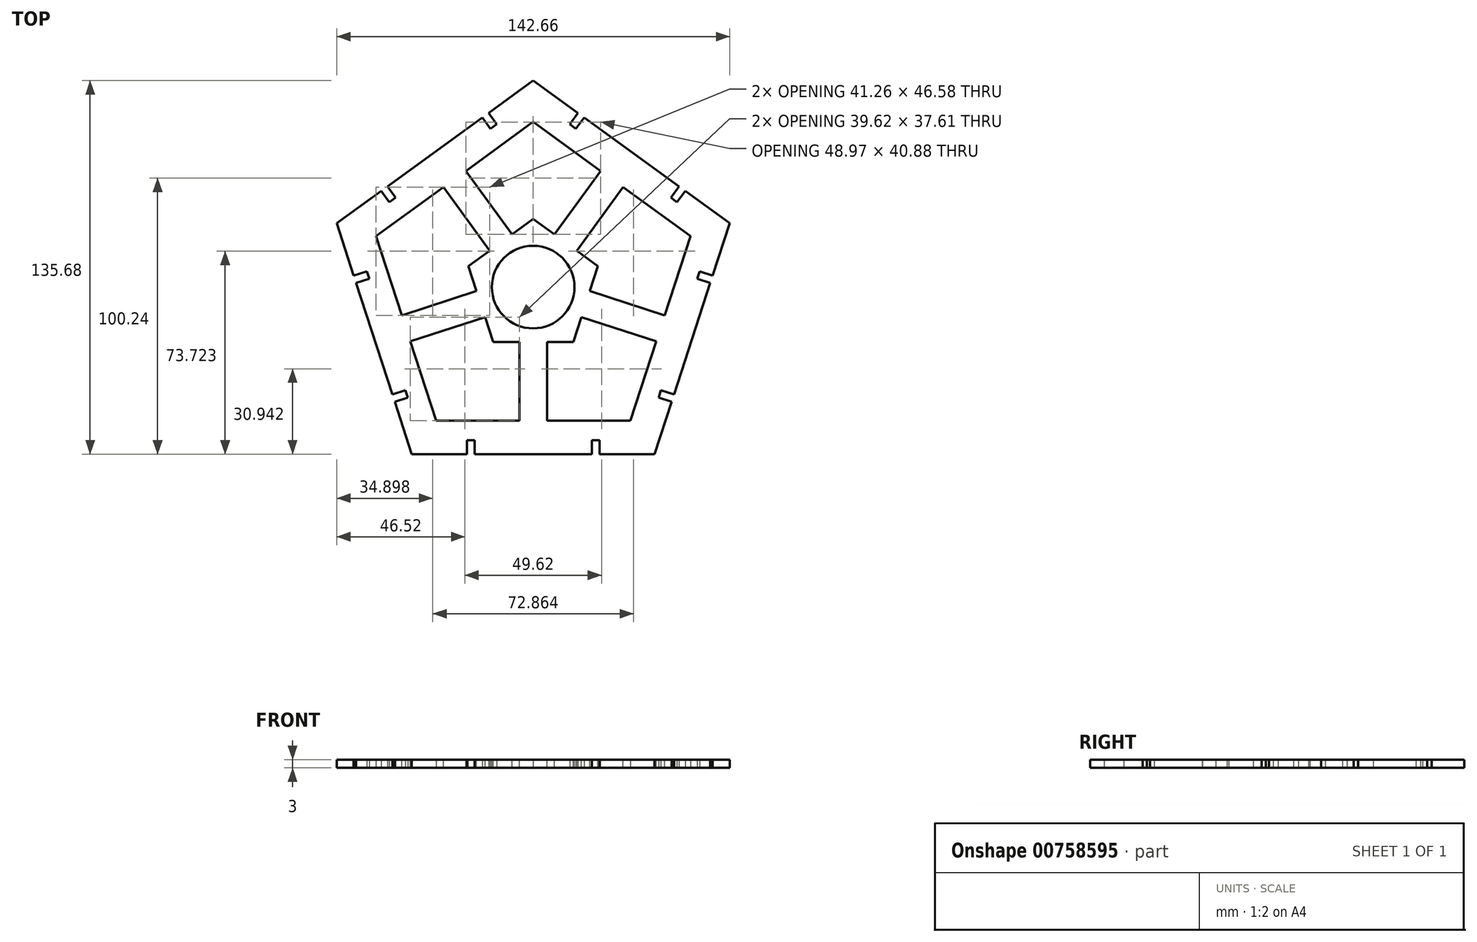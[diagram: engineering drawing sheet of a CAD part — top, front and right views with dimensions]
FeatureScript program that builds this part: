
annotation { "Feature Type Name" : "Feature", "Feature Type Description" : "" }
export const myFeature = defineFeature(function(context is Context, id is Id, definition is map)
    precondition{}
    {
        {
            var Q0;
            Q0=qCreatedBy(makeId("Top.planeOp"),FACE);
            var sketch = newSketch(context, id + "F0", { "sketchPlane" : qUnion([Q0])});
            skCircle(sketch, "E0.cCircle", {"center": v(0, 0) * mm, "radius": 75 * mm, "construction": true});
            skLineSegment(sketch, "E0.0", {"start": v(0, 75) * mm, "end": v(16.18, 63.24) * mm});
            skLineSegment(sketch, "E0.1", {"start": v(71.33, 23.18) * mm, "end": v(65.15, 4.16) * mm});
            skLineSegment(sketch, "E0.2", {"start": v(44.08, -60.68) * mm, "end": v(24.08, -60.68) * mm});
            skLineSegment(sketch, "E0.3", {"start": v(-44.08, -60.68) * mm, "end": v(-50.26, -41.66) * mm});
            skLineSegment(sketch, "E0.4", {"start": v(-71.33, 23.18) * mm, "end": v(-55.15, 34.93) * mm});
            skLineSegment(sketch, "E1", {"start": v(-16.18, 63.24) * mm, "end": v(-13.24, 59.2) * mm});
            skLineSegment(sketch, "E2", {"start": v(-13.24, 59.2) * mm, "end": v(-15.5, 57.55) * mm});
            skLineSegment(sketch, "E3", {"start": v(-15.5, 57.55) * mm, "end": v(-18.45, 61.6) * mm});
            skLineSegment(sketch, "E4", {"start": v(-35.66, 49.09) * mm, "end": v(44.08, -60.68) * mm, "construction": true});
            skLineSegment(sketch, "E5", {"start": v(-44.08, -60.68) * mm, "end": v(35.66, 49.09) * mm, "construction": true});
            skLineSegment(sketch, "E6", {"start": v(-71.33, 23.18) * mm, "end": v(57.7, -18.75) * mm, "construction": true});
            skLineSegment(sketch, "E7", {"start": v(71.33, 23.18) * mm, "end": v(-57.7, -18.75) * mm, "construction": true});
            skLineSegment(sketch, "E8", {"start": v(0, 75) * mm, "end": v(0, -60.68) * mm, "construction": true});
            skLineSegment(sketch, "E9.trimOffspring", {"start": v(-16.18, 63.24) * mm, "end": v(0, 75) * mm});
            skLineSegment(sketch, "E10.MirrorCS", {"start": v(-55.15, 34.93) * mm, "end": v(-52.2, 30.89) * mm});
            skLineSegment(sketch, "E11.MirrorCS", {"start": v(-49.94, 32.53) * mm, "end": v(-52.88, 36.58) * mm});
            skLineSegment(sketch, "E12.MirrorCS", {"start": v(-52.2, 30.89) * mm, "end": v(-49.94, 32.53) * mm});
            skLineSegment(sketch, "E13.trimOffspring", {"start": v(-52.88, 36.58) * mm, "end": v(-18.45, 61.6) * mm});
            skLineSegment(sketch, "E14.1.0", {"start": v(-65.15, 4.16) * mm, "end": v(-60.4, 5.7) * mm});
            skLineSegment(sketch, "E14.1.1", {"start": v(-59.53, 3.04) * mm, "end": v(-64.28, 1.5) * mm});
            skLineSegment(sketch, "E14.1.2", {"start": v(-60.4, 5.7) * mm, "end": v(-59.53, 3.04) * mm});
            skLineSegment(sketch, "E14.1.3", {"start": v(-46.37, -37.45) * mm, "end": v(-51.13, -39) * mm});
            skLineSegment(sketch, "E14.1.4", {"start": v(-45.5, -40.11) * mm, "end": v(-46.37, -37.45) * mm});
            skLineSegment(sketch, "E14.1.5", {"start": v(-50.26, -41.66) * mm, "end": v(-45.5, -40.11) * mm});
            skLineSegment(sketch, "E14.2.0", {"start": v(-24.08, -60.68) * mm, "end": v(-24.08, -55.68) * mm});
            skLineSegment(sketch, "E14.2.1", {"start": v(-21.28, -55.68) * mm, "end": v(-21.28, -60.68) * mm});
            skLineSegment(sketch, "E14.2.2", {"start": v(-24.08, -55.68) * mm, "end": v(-21.28, -55.68) * mm});
            skLineSegment(sketch, "E14.2.3", {"start": v(21.28, -55.68) * mm, "end": v(21.28, -60.68) * mm});
            skLineSegment(sketch, "E14.2.4", {"start": v(24.08, -55.68) * mm, "end": v(21.28, -55.68) * mm});
            skLineSegment(sketch, "E14.2.5", {"start": v(24.08, -60.68) * mm, "end": v(24.08, -55.68) * mm});
            skLineSegment(sketch, "E14.3.0", {"start": v(50.26, -41.66) * mm, "end": v(45.5, -40.11) * mm});
            skLineSegment(sketch, "E14.3.1", {"start": v(46.37, -37.45) * mm, "end": v(51.13, -39) * mm});
            skLineSegment(sketch, "E14.3.2", {"start": v(45.5, -40.11) * mm, "end": v(46.37, -37.45) * mm});
            skLineSegment(sketch, "E14.3.3", {"start": v(59.53, 3.04) * mm, "end": v(64.28, 1.5) * mm});
            skLineSegment(sketch, "E14.3.4", {"start": v(60.4, 5.7) * mm, "end": v(59.53, 3.04) * mm});
            skLineSegment(sketch, "E14.3.5", {"start": v(65.15, 4.16) * mm, "end": v(60.4, 5.7) * mm});
            skLineSegment(sketch, "E14.4.0", {"start": v(55.15, 34.93) * mm, "end": v(52.2, 30.89) * mm});
            skLineSegment(sketch, "E14.4.1", {"start": v(49.94, 32.53) * mm, "end": v(52.88, 36.58) * mm});
            skLineSegment(sketch, "E14.4.2", {"start": v(52.2, 30.89) * mm, "end": v(49.94, 32.53) * mm});
            skLineSegment(sketch, "E14.4.3", {"start": v(15.5, 57.55) * mm, "end": v(18.45, 61.6) * mm});
            skLineSegment(sketch, "E14.4.4", {"start": v(13.24, 59.2) * mm, "end": v(15.5, 57.55) * mm});
            skLineSegment(sketch, "E14.4.5", {"start": v(16.18, 63.24) * mm, "end": v(13.24, 59.2) * mm});
            skLineSegment(sketch, "E15.trimOffspring", {"start": v(-65.15, 4.16) * mm, "end": v(-71.33, 23.18) * mm});
            skLineSegment(sketch, "E16.trimOffspring", {"start": v(21.28, -60.68) * mm, "end": v(-21.28, -60.68) * mm});
            skLineSegment(sketch, "E17.trimOffspring", {"start": v(-24.08, -60.68) * mm, "end": v(-44.08, -60.68) * mm});
            skLineSegment(sketch, "E18.trimOffspring", {"start": v(-51.13, -39) * mm, "end": v(-64.28, 1.5) * mm});
            skLineSegment(sketch, "E19.trimOffspring", {"start": v(18.45, 61.6) * mm, "end": v(52.88, 36.58) * mm});
            skLineSegment(sketch, "E20.trimOffspring", {"start": v(55.15, 34.93) * mm, "end": v(71.33, 23.18) * mm});
            skLineSegment(sketch, "E21.trimOffspring", {"start": v(64.28, 1.5) * mm, "end": v(51.13, -39) * mm});
            skLineSegment(sketch, "E22.trimOffspring", {"start": v(50.26, -41.66) * mm, "end": v(44.08, -60.68) * mm});
            skCircle(sketch, "E23.cCircle", {"center": v(0, 0) * mm, "radius": 60 * mm, "construction": true});
            skLineSegment(sketch, "E23.0", {"start": v(0, 60) * mm, "end": v(57.06, 18.54) * mm});
            skLineSegment(sketch, "E23.1", {"start": v(57.06, 18.54) * mm, "end": v(35.27, -48.54) * mm});
            skLineSegment(sketch, "E23.2", {"start": v(35.27, -48.54) * mm, "end": v(-35.27, -48.54) * mm});
            skLineSegment(sketch, "E23.3", {"start": v(-35.27, -48.54) * mm, "end": v(-57.06, 18.54) * mm});
            skLineSegment(sketch, "E23.4", {"start": v(-57.06, 18.54) * mm, "end": v(0, 60) * mm});
            skSolve(sketch);
        }
        {
            var Q0;
            Q0=qSketchRegion(id+"F0",true);
            extrude(context, id + "F1", {"entities" : qUnion([Q0]), "depth" : 3 * mm, "offsetDistance" : 25 * mm});
        }
        {
            var Q0;
            Q0=makeQuery(id+"F7oamPH84VVUofO_3.boolean.opBoolean","MERGE",FACE,{"derivedFrom":[makeQuery(id+"F9TRZGhlL7vivvJ_2.boolean.opBoolean","MERGE",FACE,{"derivedFrom":[makeQuery(id+"FcwpvQgZIup3No6_1.boolean.opBoolean","MERGE",FACE,{"derivedFrom":[makeQuery(id+"F1.opExtrude","CAP_FACE",FACE,{"disambiguationData":[OSD([sQuery(id+"F0.wireOp",EDGE,"E0.0"),sQuery(id+"F0.wireOp",EDGE,"E0.1"),sQuery(id+"F0.wireOp",EDGE,"E0.2"),sQuery(id+"F0.wireOp",EDGE,"E0.3"),sQuery(id+"F0.wireOp",EDGE,"E0.4"),sQuery(id+"F0.wireOp",EDGE,"E1"),sQuery(id+"F0.wireOp",EDGE,"E2"),sQuery(id+"F0.wireOp",EDGE,"E3"),sQuery(id+"F0.wireOp",EDGE,"E9.trimOffspring"),sQuery(id+"F0.wireOp",EDGE,"E10.MirrorCS"),sQuery(id+"F0.wireOp",EDGE,"E11.MirrorCS"),sQuery(id+"F0.wireOp",EDGE,"E12.MirrorCS"),sQuery(id+"F0.wireOp",EDGE,"E13.trimOffspring"),sQuery(id+"F0.wireOp",EDGE,"E14.1.0"),sQuery(id+"F0.wireOp",EDGE,"E14.1.1"),sQuery(id+"F0.wireOp",EDGE,"E14.1.2"),sQuery(id+"F0.wireOp",EDGE,"E14.1.3"),sQuery(id+"F0.wireOp",EDGE,"E14.1.4"),sQuery(id+"F0.wireOp",EDGE,"E14.1.5"),sQuery(id+"F0.wireOp",EDGE,"E14.2.0"),sQuery(id+"F0.wireOp",EDGE,"E14.2.1"),sQuery(id+"F0.wireOp",EDGE,"E14.2.2"),sQuery(id+"F0.wireOp",EDGE,"E14.2.3"),sQuery(id+"F0.wireOp",EDGE,"E14.2.4"),sQuery(id+"F0.wireOp",EDGE,"E14.2.5"),sQuery(id+"F0.wireOp",EDGE,"E14.3.0"),sQuery(id+"F0.wireOp",EDGE,"E14.3.1"),sQuery(id+"F0.wireOp",EDGE,"E14.3.2"),sQuery(id+"F0.wireOp",EDGE,"E14.3.3"),sQuery(id+"F0.wireOp",EDGE,"E14.3.4"),sQuery(id+"F0.wireOp",EDGE,"E14.3.5"),sQuery(id+"F0.wireOp",EDGE,"E14.4.0"),sQuery(id+"F0.wireOp",EDGE,"E14.4.1"),sQuery(id+"F0.wireOp",EDGE,"E14.4.2"),sQuery(id+"F0.wireOp",EDGE,"E14.4.3"),sQuery(id+"F0.wireOp",EDGE,"E14.4.4"),sQuery(id+"F0.wireOp",EDGE,"E14.4.5"),sQuery(id+"F0.wireOp",EDGE,"E15.trimOffspring"),sQuery(id+"F0.wireOp",EDGE,"E16.trimOffspring"),sQuery(id+"F0.wireOp",EDGE,"E17.trimOffspring"),sQuery(id+"F0.wireOp",EDGE,"E18.trimOffspring"),sQuery(id+"F0.wireOp",EDGE,"E19.trimOffspring"),sQuery(id+"F0.wireOp",EDGE,"E20.trimOffspring"),sQuery(id+"F0.wireOp",EDGE,"E21.trimOffspring"),sQuery(id+"F0.wireOp",EDGE,"E22.trimOffspring"),sQuery(id+"F0.wireOp",EDGE,"E23.0"),sQuery(id+"F0.wireOp",EDGE,"E23.1"),sQuery(id+"F0.wireOp",EDGE,"E23.2"),sQuery(id+"F0.wireOp",EDGE,"E23.3"),sQuery(id+"F0.wireOp",EDGE,"E23.4")])],"isStart":false}),makeQuery(id+"FcwpvQgZIup3No6_1.opExtrude","CAP_FACE",FACE,{"disambiguationData":[OSD([sQuery(id+"FsdsBESLdJ1JIvc_1.wireOp",EDGE,"de833a3a-313a-4596-8202-035c041a42ca.0"),sQuery(id+"FsdsBESLdJ1JIvc_1.wireOp",EDGE,"de833a3a-313a-4596-8202-035c041a42ca.1"),sQuery(id+"FsdsBESLdJ1JIvc_1.wireOp",EDGE,"de833a3a-313a-4596-8202-035c041a42ca.2"),sQuery(id+"FsdsBESLdJ1JIvc_1.wireOp",EDGE,"de833a3a-313a-4596-8202-035c041a42ca.3"),sQuery(id+"FsdsBESLdJ1JIvc_1.wireOp",EDGE,"de833a3a-313a-4596-8202-035c041a42ca.4"),sQuery(id+"FsdsBESLdJ1JIvc_1.wireOp",EDGE,"a308593b-41e8-415b-b94c-e11fd7466d5a.0"),sQuery(id+"FsdsBESLdJ1JIvc_1.wireOp",EDGE,"a308593b-41e8-415b-b94c-e11fd7466d5a.1"),sQuery(id+"FsdsBESLdJ1JIvc_1.wireOp",EDGE,"a308593b-41e8-415b-b94c-e11fd7466d5a.2"),sQuery(id+"FsdsBESLdJ1JIvc_1.wireOp",EDGE,"a308593b-41e8-415b-b94c-e11fd7466d5a.3"),sQuery(id+"FsdsBESLdJ1JIvc_1.wireOp",EDGE,"a308593b-41e8-415b-b94c-e11fd7466d5a.4")])],"isStart":true})]}),makeQuery(id+"F9TRZGhlL7vivvJ_2.opExtrude","CAP_FACE",FACE,{"disambiguationData":[OSD([sQuery(id+"Ff6WRs0W7eyaktz_2.wireOp",EDGE,"6beabe26-07f1-4b03-9cb5-d80d9ebc594f.0"),sQuery(id+"Ff6WRs0W7eyaktz_2.wireOp",EDGE,"6beabe26-07f1-4b03-9cb5-d80d9ebc594f.1"),sQuery(id+"Ff6WRs0W7eyaktz_2.wireOp",EDGE,"6beabe26-07f1-4b03-9cb5-d80d9ebc594f.2"),sQuery(id+"Ff6WRs0W7eyaktz_2.wireOp",EDGE,"6beabe26-07f1-4b03-9cb5-d80d9ebc594f.3"),sQuery(id+"Ff6WRs0W7eyaktz_2.wireOp",EDGE,"6beabe26-07f1-4b03-9cb5-d80d9ebc594f.4"),sQuery(id+"Ff6WRs0W7eyaktz_2.wireOp",EDGE,"313384f4-31bd-43dd-b64d-91ce542deea2.0"),sQuery(id+"Ff6WRs0W7eyaktz_2.wireOp",EDGE,"313384f4-31bd-43dd-b64d-91ce542deea2.1"),sQuery(id+"Ff6WRs0W7eyaktz_2.wireOp",EDGE,"313384f4-31bd-43dd-b64d-91ce542deea2.2"),sQuery(id+"Ff6WRs0W7eyaktz_2.wireOp",EDGE,"313384f4-31bd-43dd-b64d-91ce542deea2.3"),sQuery(id+"Ff6WRs0W7eyaktz_2.wireOp",EDGE,"313384f4-31bd-43dd-b64d-91ce542deea2.4")])],"isStart":true})]}),makeQuery(id+"F7oamPH84VVUofO_3.opExtrude","CAP_FACE",FACE,{"disambiguationData":[OSD([sQuery(id+"FCtNTOOhJTabHIr_3.wireOp",EDGE,"ce65d7c0-cc87-4925-8475-852a1e82e0af.0"),sQuery(id+"FCtNTOOhJTabHIr_3.wireOp",EDGE,"ce65d7c0-cc87-4925-8475-852a1e82e0af.1"),sQuery(id+"FCtNTOOhJTabHIr_3.wireOp",EDGE,"ce65d7c0-cc87-4925-8475-852a1e82e0af.2"),sQuery(id+"FCtNTOOhJTabHIr_3.wireOp",EDGE,"ce65d7c0-cc87-4925-8475-852a1e82e0af.3"),sQuery(id+"FCtNTOOhJTabHIr_3.wireOp",EDGE,"ce65d7c0-cc87-4925-8475-852a1e82e0af.4"),sQuery(id+"FCtNTOOhJTabHIr_3.wireOp",EDGE,"5047fc87-8845-4384-a8f3-4e3b16de0bd1.0"),sQuery(id+"FCtNTOOhJTabHIr_3.wireOp",EDGE,"5047fc87-8845-4384-a8f3-4e3b16de0bd1.1"),sQuery(id+"FCtNTOOhJTabHIr_3.wireOp",EDGE,"5047fc87-8845-4384-a8f3-4e3b16de0bd1.2"),sQuery(id+"FCtNTOOhJTabHIr_3.wireOp",EDGE,"5047fc87-8845-4384-a8f3-4e3b16de0bd1.3"),sQuery(id+"FCtNTOOhJTabHIr_3.wireOp",EDGE,"5047fc87-8845-4384-a8f3-4e3b16de0bd1.4")])],"isStart":true})]});
            var sketch = newSketch(context, id + "F2", { "sketchPlane" : qUnion([Q0])});
            skLineSegment(sketch, "E24.0", {"start": v(14.53, -20) * mm, "end": v(5, -20) * mm});
            skLineSegment(sketch, "E24.1", {"start": v(-14.53, -20) * mm, "end": v(-17.48, -10.94) * mm});
            skLineSegment(sketch, "E24.2", {"start": v(-23.51, 7.64) * mm, "end": v(-15.8, 13.24) * mm});
            skLineSegment(sketch, "E24.3", {"start": v(0, 24.72) * mm, "end": v(7.71, 19.12) * mm});
            skLineSegment(sketch, "E24.4", {"start": v(23.51, 7.64) * mm, "end": v(20.57, -1.43) * mm});
            skPoint(sketch, "E24.0.midPoint", {"position": v(0, -20) * mm});
            skCircle(sketch, "E25", {"center": v(0, 0) * mm, "radius": 15 * mm});
            skLineSegment(sketch, "E26", {"start": v(-11.76, 16.18) * mm, "end": v(-28.53, 39.27) * mm, "construction": true});
            skLineSegment(sketch, "E27", {"start": v(-7.71, 19.12) * mm, "end": v(-24.49, 42.2) * mm});
            skLineSegment(sketch, "E28.MirrorCS", {"start": v(-15.8, 13.24) * mm, "end": v(-32.58, 36.33) * mm});
            skLineSegment(sketch, "E29", {"start": v(-24.49, 42.2) * mm, "end": v(-32.58, 36.33) * mm});
            skLineSegment(sketch, "E30.trimOffspring", {"start": v(-7.71, 19.12) * mm, "end": v(0, 24.72) * mm});
            skLineSegment(sketch, "E31.1.0", {"start": v(-20.57, -1.43) * mm, "end": v(-47.71, -10.24) * mm});
            skLineSegment(sketch, "E31.1.1", {"start": v(-17.48, -10.94) * mm, "end": v(-44.62, -19.76) * mm});
            skLineSegment(sketch, "E31.1.2", {"start": v(-47.71, -10.24) * mm, "end": v(-44.62, -19.76) * mm});
            skCircle(sketch, "E31.1.3", {"center": v(0, 0) * mm, "radius": 20 * mm, "construction": true});
            skLineSegment(sketch, "E31.2.0", {"start": v(-5, -20) * mm, "end": v(-5, -48.54) * mm});
            skLineSegment(sketch, "E31.2.1", {"start": v(5, -20) * mm, "end": v(5, -48.54) * mm});
            skLineSegment(sketch, "E31.2.2", {"start": v(-5, -48.54) * mm, "end": v(5, -48.54) * mm});
            skLineSegment(sketch, "E31.3.0", {"start": v(17.48, -10.94) * mm, "end": v(44.62, -19.76) * mm});
            skLineSegment(sketch, "E31.3.1", {"start": v(20.57, -1.43) * mm, "end": v(47.71, -10.24) * mm});
            skLineSegment(sketch, "E31.3.2", {"start": v(44.62, -19.76) * mm, "end": v(47.71, -10.24) * mm});
            skArc(sketch, "E31.3.3", {"start": v(-11.76, 16.18) * mm, "mid": v(-19.75, 3.13) * mm, "end": v(-16.18, -11.76) * mm, "construction": true});
            skLineSegment(sketch, "E31.4.0", {"start": v(15.8, 13.24) * mm, "end": v(32.58, 36.33) * mm});
            skLineSegment(sketch, "E31.4.1", {"start": v(7.71, 19.12) * mm, "end": v(24.49, 42.2) * mm});
            skLineSegment(sketch, "E31.4.2", {"start": v(32.58, 36.33) * mm, "end": v(24.49, 42.2) * mm});
            skLineSegment(sketch, "E32.trimOffspring", {"start": v(15.8, 13.24) * mm, "end": v(23.51, 7.64) * mm});
            skLineSegment(sketch, "E33.trimOffspring", {"start": v(17.48, -10.94) * mm, "end": v(14.53, -20) * mm});
            skLineSegment(sketch, "E34.trimOffspring", {"start": v(-5, -20) * mm, "end": v(-14.53, -20) * mm});
            skLineSegment(sketch, "E35.trimOffspring", {"start": v(-20.57, -1.43) * mm, "end": v(-23.51, 7.64) * mm});
            skSolve(sketch);
        }
        {
            var Q0;
            Q0=qSketchRegion(id+"F2",true);
            extrude(context, id + "F3", {"entities" : qUnion([Q0]), "operationType" : NewBodyOperationType.ADD, "oppositeDirection" : true, "depth" : 3 * mm, "offsetDistance" : 25 * mm});
        }
    });
